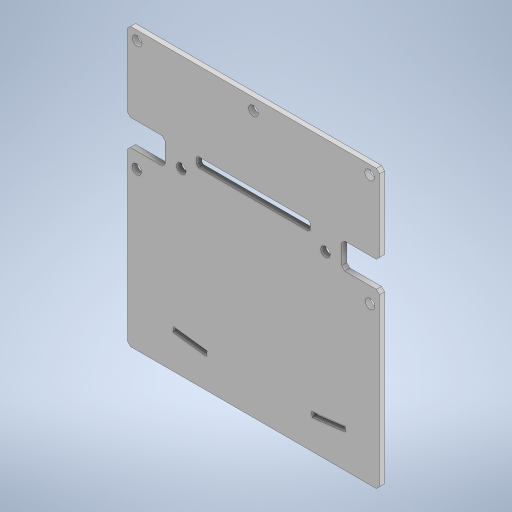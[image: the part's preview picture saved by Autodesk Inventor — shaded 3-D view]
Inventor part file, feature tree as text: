
AUTODESK INVENTOR PART (.ipt)
format: ipt  version: 2023 (Build 270158000, 158)  size: 424,448 bytes
history: native  units: in
note: dims shown in document units (in); Inventor stores cm internally (conversion verified against a paired STEP export)
features: reference x24, other x10, extrude x10, sketch x10, projected_geometry x7, chamfer x2
ambient origin geometry x8: Origin, YZ Plane, XZ Plane, XY Plane, X Axis, Y Axis, Z Axis, Center Point
bodies: Body1 (feature_tree)
feature tree (63):
  other  "Bryła1"
  extrude  "Wyciągnięcie proste1"  Depth=0.0787in
  extrude  "Wyciągnięcie proste2"  Depth=0.0787in
  extrude  "Wyciągnięcie proste3"  Depth=0.0787in
  extrude  "Wyciągnięcie proste4"  Depth=0.0787in
  extrude  "Wyciągnięcie proste5"  Depth=0.063in TaperAngle=0.0deg
  extrude  "Wyciągnięcie proste6"  Depth=0.315in TaperAngle=0.0deg
  extrude  "Wyciągnięcie proste7"  Depth=0.3937in
  extrude  "Wyciągnięcie proste8"  Depth=0.2756in
  extrude  "Wyciągnięcie proste9"  Depth=0.3937in
  extrude  "Wyciągnięcie proste10"  Depth=0.3937in TaperAngle=0.0deg
  chamfer  "Faza1"  Distance=0.3937in
  chamfer  "Faza2"  Distance=0.1969in
  sketch  "Szkic1"
  reference  "Odniesienie1"
  reference  "Odniesienie2"
  reference  "Odniesienie3"
  reference  "Odniesienie4"
  reference  "Odniesienie5"
  reference  "Odniesienie6"
  reference  "Odniesienie7"
  reference  "Odniesienie8"
  reference  "Odniesienie9"
  reference  "Odniesienie10"
  reference  "Odniesienie11"
  reference  "Odniesienie12"
  reference  "Odniesienie13"
  reference  "Odniesienie14"
  reference  "Odniesienie15"
  reference  "Odniesienie16"
  sketch  "Szkic2"
  projected_geometry  "Pętla rzutowana1"
  sketch  "Szkic3"
  projected_geometry  "Pętla rzutowana2"
  sketch  "Szkic4"
  projected_geometry  "Pętla rzutowana3"
  sketch  "Szkic5"
  projected_geometry  "Pętla rzutowana4"
  sketch  "Szkic6"
  projected_geometry  "Pętla rzutowana5"
  sketch  "Szkic7"
  reference  "Odniesienie17"
  reference  "Odniesienie18"
  reference  "Odniesienie19"
  reference  "Odniesienie20"
  reference  "Odniesienie21"
  reference  "Odniesienie22"
  reference  "Odniesienie23"
  reference  "Odniesienie24"
  sketch  "Szkic8"
  projected_geometry  "Pętla rzutowana6"
  sketch  "Szkic9"
  projected_geometry  "Pętla rzutowana7"
  sketch  "Szkic10"
  other  "Zespół3"
  other  "uchwyt_na_silnik:1"
  other  "SCIANA_2.0_MIR:1"
  other  "SCIANA_2.0:1"
  other  "minisumopodsr:1"
  other  "<userpath>\Desktop\MojeRoboty\Stefan\mechanics\STEFAN_2.0.iam"
  other  "STEFAN_2.0.iam"
  other  "TOF_VLCOS:4"
  other  "TOF_VLCOS:3"
